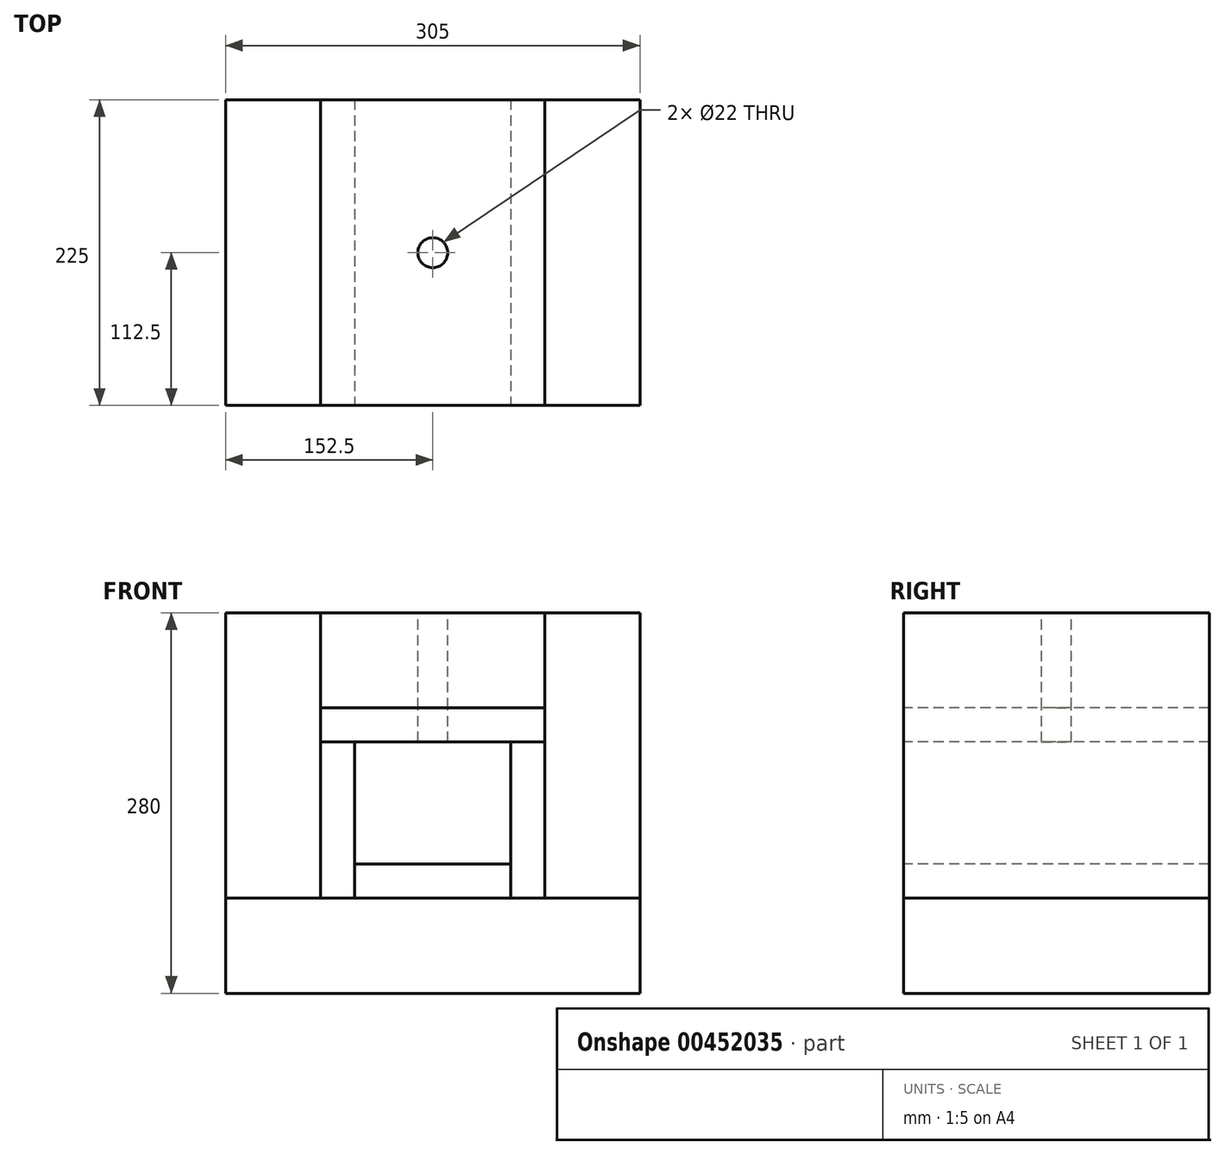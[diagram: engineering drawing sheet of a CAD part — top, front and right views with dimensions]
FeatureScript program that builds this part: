
annotation { "Feature Type Name" : "Feature", "Feature Type Description" : "" }
export const myFeature = defineFeature(function(context is Context, id is Id, definition is map)
    precondition{}
    {
        {
            var Q0;
            Q0=qCreatedBy(makeId("Front.planeOp"),FACE);
            var sketch = newSketch(context, id + "F0", { "sketchPlane" : qUnion([Q0])});
            skLineSegment(sketch, "E0.bottom", {"start": v(0, 0) * mm, "end": v(115, 0) * mm});
            skLineSegment(sketch, "E0.top", {"start": v(0, 25) * mm, "end": v(115, 25) * mm});
            skLineSegment(sketch, "E0.left", {"start": v(0, 0) * mm, "end": v(0, 25) * mm});
            skLineSegment(sketch, "E0.right", {"start": v(115, 0) * mm, "end": v(115, 25) * mm});
            skSolve(sketch);
        }
        {
            var Q0;
            Q0 = qSketchRegion(id + "F0", true);
            extrude(context, id + "F1", {"entities" : qUnion([Q0]), "oppositeDirection" : true, "depth" : 225 * mm, "offsetDistance" : 25 * mm});
        }
        {
            var Q0;
            Q0=qCreatedBy(makeId("Front.planeOp"),FACE);
            var sketch = newSketch(context, id + "F2", { "sketchPlane" : qUnion([Q0])});
            skLineSegment(sketch, "E1.bottom", {"start": v(0, 0) * mm, "end": v(-25, 0) * mm});
            skLineSegment(sketch, "E1.top", {"start": v(0, 115) * mm, "end": v(-25, 115) * mm});
            skLineSegment(sketch, "E1.left", {"start": v(0, 0) * mm, "end": v(0, 115) * mm});
            skLineSegment(sketch, "E1.right", {"start": v(-25, 0) * mm, "end": v(-25, 115) * mm});
            skSolve(sketch);
        }
        {
            var Q0;
            Q0 = qSketchRegion(id + "F2", true);
            var Q1;
            Q1=makeQuery(id+"F1.opExtrude","CAP_FACE",FACE,{"disambiguationData":[OSD([sQuery(id+"F0.wireOp",EDGE,"E0.bottom"),sQuery(id+"F0.wireOp",EDGE,"E0.top"),sQuery(id+"F0.wireOp",EDGE,"E0.left"),sQuery(id+"F0.wireOp",EDGE,"E0.right")])],"isStart":false});
            extrude(context, id + "F3", {"entities" : qUnion([Q0]), "endBound" : BoundingType.UP_TO_SURFACE, "oppositeDirection" : true, "endBoundEntityFace" : qUnion([Q1]), "depth" : 230 * mm, "offsetDistance" : 25 * mm});
        }
        {
            var Q0;
            Q0=makeQuery(id+"F1.opExtrude","SWEPT_FACE",FACE,{"disambiguationData":[OSD([sQuery(id+"F0.wireOp",EDGE,"E0.right")])]});
            var Q1;
            Q1=makeQuery(id+"F1.opExtrude","SWEPT_FACE",FACE,{"disambiguationData":[OSD([sQuery(id+"F0.wireOp",EDGE,"E0.left")])]});
            cPlane(context, id + "F4", {"entities" : qUnion([Q0, Q1]), "cplaneType" : CPlaneType.MID_PLANE, "offset" : 25 * mm, "width" : 150 * mm, "height" : 150 * mm});
        }
        {
            var Q0;
            Q0=makeQuery(id+"F3.opExtrude","SWEPT_BODY",BODY,{"disambiguationData":[OSD([sQuery(id+"F2.wireOp",EDGE,"E1.bottom"),sQuery(id+"F2.wireOp",EDGE,"E1.top"),sQuery(id+"F2.wireOp",EDGE,"E1.left"),sQuery(id+"F2.wireOp",EDGE,"E1.right")])]});
            var Q1;
            Q1=qCreatedBy(id+"F4.planeOp",FACE);
            mirror(context, id + "F5", {"entities" : qUnion([Q0]), "mirrorPlane" : qUnion([Q1])});
        }
        {
            var Q0;
            Q0=qCreatedBy(makeId("Front.planeOp"),FACE);
            var sketch = newSketch(context, id + "F6", { "sketchPlane" : qUnion([Q0])});
            skPoint(sketch, "E2.0", {"position": v(-25, 115) * mm});
            skPoint(sketch, "E3.0", {"position": v(140, 115) * mm});
            skLineSegment(sketch, "E4.bottom", {"start": v(-25, 115) * mm, "end": v(140, 115) * mm});
            skLineSegment(sketch, "E4.top", {"start": v(-25, 140) * mm, "end": v(140, 140) * mm});
            skLineSegment(sketch, "E4.left", {"start": v(-25, 115) * mm, "end": v(-25, 140) * mm});
            skLineSegment(sketch, "E4.right", {"start": v(140, 115) * mm, "end": v(140, 140) * mm});
            skSolve(sketch);
        }
        {
            var Q0;
            Q0 = qSketchRegion(id + "F6", true);
            var Q1;
            Q1=makeQuery(id+"F1.opExtrude","CAP_FACE",FACE,{"disambiguationData":[OSD([sQuery(id+"F0.wireOp",EDGE,"E0.bottom"),sQuery(id+"F0.wireOp",EDGE,"E0.top"),sQuery(id+"F0.wireOp",EDGE,"E0.left"),sQuery(id+"F0.wireOp",EDGE,"E0.right")])],"isStart":false});
            extrude(context, id + "F7", {"entities" : qUnion([Q0]), "endBound" : BoundingType.UP_TO_SURFACE, "oppositeDirection" : true, "endBoundEntityFace" : qUnion([Q1]), "depth" : 230 * mm, "offsetDistance" : 25 * mm});
        }
        {
            var Q0;
            Q0=qCreatedBy(makeId("Front.planeOp"),FACE);
            var sketch = newSketch(context, id + "F8", { "sketchPlane" : qUnion([Q0])});
            skLineSegment(sketch, "E5.bottom", {"start": v(-95, 0) * mm, "end": v(210, 0) * mm});
            skLineSegment(sketch, "E5.top", {"start": v(-95, -70) * mm, "end": v(210, -70) * mm});
            skLineSegment(sketch, "E5.left", {"start": v(-95, 0) * mm, "end": v(-95, -70) * mm});
            skLineSegment(sketch, "E5.right", {"start": v(210, 0) * mm, "end": v(210, -70) * mm});
            skPoint(sketch, "E6.0", {"position": v(-25, 0) * mm});
            skPoint(sketch, "E7.0", {"position": v(140, 0) * mm});
            skSolve(sketch);
        }
        {
            var Q0;
            Q0 = qSketchRegion(id + "F8", true);
            var Q1;
            Q1=makeQuery(id+"F1.opExtrude","CAP_FACE",FACE,{"disambiguationData":[OSD([sQuery(id+"F0.wireOp",EDGE,"E0.bottom"),sQuery(id+"F0.wireOp",EDGE,"E0.top"),sQuery(id+"F0.wireOp",EDGE,"E0.left"),sQuery(id+"F0.wireOp",EDGE,"E0.right")])],"isStart":false});
            extrude(context, id + "F9", {"entities" : qUnion([Q0]), "endBound" : BoundingType.UP_TO_SURFACE, "oppositeDirection" : true, "endBoundEntityFace" : qUnion([Q1]), "depth" : 25 * mm});
        }
        {
            var Q0;
            Q0=qCreatedBy(makeId("Front.planeOp"),FACE);
            var sketch = newSketch(context, id + "F10", { "sketchPlane" : qUnion([Q0])});
            skPoint(sketch, "E8.0", {"position": v(-25, 0) * mm});
            skPoint(sketch, "E9.0", {"position": v(-25, 140) * mm});
            skPoint(sketch, "E10.0", {"position": v(-95, 0) * mm});
            skLineSegment(sketch, "E11.bottom", {"start": v(-95, 0) * mm, "end": v(-25, 0) * mm});
            skLineSegment(sketch, "E11.top", {"start": v(-95, 210) * mm, "end": v(-25, 210) * mm});
            skLineSegment(sketch, "E11.left", {"start": v(-95, 0) * mm, "end": v(-95, 210) * mm});
            skLineSegment(sketch, "E11.right", {"start": v(-25, 0) * mm, "end": v(-25, 210) * mm});
            skSolve(sketch);
        }
        {
            var Q0;
            Q0 = qSketchRegion(id + "F10", true);
            var Q1;
            Q1=makeQuery(id+"F1.opExtrude","CAP_FACE",FACE,{"disambiguationData":[OSD([sQuery(id+"F0.wireOp",EDGE,"E0.bottom"),sQuery(id+"F0.wireOp",EDGE,"E0.top"),sQuery(id+"F0.wireOp",EDGE,"E0.left"),sQuery(id+"F0.wireOp",EDGE,"E0.right")])],"isStart":false});
            extrude(context, id + "F11", {"entities" : qUnion([Q0]), "endBound" : BoundingType.UP_TO_SURFACE, "oppositeDirection" : true, "endBoundEntityFace" : qUnion([Q1]), "depth" : 25 * mm});
        }
        {
            var Q0;
            Q0=makeQuery(id+"F11.opExtrude","SWEPT_BODY",BODY,{"disambiguationData":[OSD([sQuery(id+"F10.wireOp",EDGE,"E11.bottom"),sQuery(id+"F10.wireOp",EDGE,"E11.top"),sQuery(id+"F10.wireOp",EDGE,"E11.left"),sQuery(id+"F10.wireOp",EDGE,"E11.right")])]});
            var Q1;
            Q1=qCreatedBy(id+"F4.planeOp",FACE);
            mirror(context, id + "F12", {"entities" : qUnion([Q0]), "mirrorPlane" : qUnion([Q1])});
        }
        {
            var Q0;
            Q0=qCreatedBy(makeId("Front.planeOp"),FACE);
            var sketch = newSketch(context, id + "F13", { "sketchPlane" : qUnion([Q0])});
            skPoint(sketch, "E12.0", {"position": v(-25, 210) * mm});
            skPoint(sketch, "E13.0", {"position": v(140, 140) * mm});
            skLineSegment(sketch, "E14.bottom", {"start": v(-25, 210) * mm, "end": v(140, 210) * mm});
            skLineSegment(sketch, "E14.top", {"start": v(-25, 140) * mm, "end": v(140, 140) * mm});
            skLineSegment(sketch, "E14.left", {"start": v(-25, 210) * mm, "end": v(-25, 140) * mm});
            skLineSegment(sketch, "E14.right", {"start": v(140, 210) * mm, "end": v(140, 140) * mm});
            skSolve(sketch);
        }
        {
            var Q0;
            Q0 = qSketchRegion(id + "F13", true);
            var Q1;
            Q1=makeQuery(id+"F1.opExtrude","CAP_FACE",FACE,{"disambiguationData":[OSD([sQuery(id+"F0.wireOp",EDGE,"E0.bottom"),sQuery(id+"F0.wireOp",EDGE,"E0.top"),sQuery(id+"F0.wireOp",EDGE,"E0.left"),sQuery(id+"F0.wireOp",EDGE,"E0.right")])],"isStart":false});
            extrude(context, id + "F14", {"entities" : qUnion([Q0]), "endBound" : BoundingType.UP_TO_SURFACE, "oppositeDirection" : true, "endBoundEntityFace" : qUnion([Q1]), "depth" : 25 * mm});
        }
        {
            var Q0;
            Q0=makeQuery(id+"F14.opExtrude","SWEPT_FACE",FACE,{"disambiguationData":[OSD([sQuery(id+"F13.wireOp",EDGE,"E14.bottom")])]});
            var sketch = newSketch(context, id + "F15", { "sketchPlane" : qUnion([Q0])});
            skPoint(sketch, "E15.0", {"position": v(57.5, 225) * mm});
            skPoint(sketch, "E16.0", {"position": v(-25, 112.5) * mm});
            skCircle(sketch, "E17", {"center": v(57.5, 112.5) * mm, "radius": 11 * mm});
            skSolve(sketch);
        }
        {
            var Q0;
            Q0 = qSketchRegion(id + "F15", true);
            var Q1;
            Q1=makeQuery(id+"F7.opExtrude","SWEPT_FACE",FACE,{"disambiguationData":[OSD([sQuery(id+"F6.wireOp",EDGE,"E4.bottom")])]});
            extrude(context, id + "F16", {"entities" : qUnion([Q0]), "operationType" : NewBodyOperationType.REMOVE, "endBound" : BoundingType.UP_TO_SURFACE, "oppositeDirection" : true, "endBoundEntityFace" : qUnion([Q1]), "depth" : 25 * mm});
        }
    });
